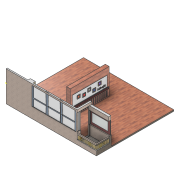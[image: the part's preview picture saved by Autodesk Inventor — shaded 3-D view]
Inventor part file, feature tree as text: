
AUTODESK INVENTOR PART (.ipt)
format: ipt  version: 2020.2 (Build 242310000, 310)  size: 1,721,344 bytes
history: native  units: mm
features: extrude x49, plane x45, sketch x36, other x4, loft x4, fillet x2, emboss x1
ambient origin geometry x8: Origin, YZ Plane, XZ Plane, XY Plane, X Axis, Y Axis, Z Axis, Center Point
bodies: Solid1 (feature_tree), Solid2 (feature_tree), Solid3 (feature_tree), Solid4 (feature_tree), Solid5 (feature_tree), Solid6 (feature_tree), Solid7 (feature_tree)
feature tree (141):
  extrude  "Extrusion1"  Depth=6000.0mm
  other  "Pod plane"
  other  "D. deo, terasa i prozori"
  plane  "Work Plane2"
  extrude  "Extrusion2"  TaperAngle=0.0deg  [1 undecoded]
  plane  "Work Plane3"
  sketch  "Sketch10"  dims[d22=100.0mm d23=100.0mm]
  extrude  "Extrusion3"  Depth=100.0mm
  extrude  "Extrusion4"  Depth=1000.0mm
  extrude  "Extrusion6"  Depth=1000.0mm
  extrude  "Extrusion7"  Depth=300.0mm
  extrude  "Extrusion8"  Depth=2000.0mm TaperAngle=0.0deg
  plane  "Work Plane4"
  plane  "Work Plane5"
  extrude  "Extrusion10"  Depth=150.0mm
  fillet  "Fillet1"  Radius=100.0mm
  plane  "Work Plane7"
  plane  "Work Plane8"
  extrude  "Extrusion11"  Depth=30.0mm
  plane  "Work Plane9"
  sketch  "Sketch15"  dims[d32=0.0mm d33=300.0mm]
  extrude  "Extrusion12"  Depth=10.0mm TaperAngle=0.0deg
  extrude  "Extrusion13"  Depth=50.0mm
  extrude  "Extrusion14"  Depth=50.0mm
  extrude  "Extrusion15"  Depth=25.0mm
  plane  "Work Plane10"
  plane  "Work Plane11"
  plane  "Work Plane12"
  sketch  "Sketch19"  dims[d93=40.0mm d94=30.0mm]
  extrude  "Extrusion18"  Depth=20.0mm TaperAngle=0.0deg
  extrude  "Extrusion19"  Depth=250.0mm TaperAngle=0.0deg
  plane  "Work Plane13"
  extrude  "Extrusion20"  TaperAngle=0.0deg  [1 undecoded]
  plane  "Work Plane14"
  extrude  "Extrusion21"  Depth=10.0mm
  plane  "Work Plane15"
  plane  "Work Plane16"
  extrude  "Extrusion22"  Depth=10.0mm
  plane  "Work Plane17"
  extrude  "Extrusion23"  Depth=200.0mm TaperAngle=0.0deg
  extrude  "Extrusion24"  TaperAngle=0.0deg  [1 undecoded]
  plane  "Work Plane18"
  plane  "Work Plane19"
  sketch  "Sketch28"  dims[d133=2.0mm d134=0.0mm d135=50.0mm]
  plane  "Work Plane20"
  extrude  "Extrusion25"  Depth=10.0mm
  extrude  "Extrusion26"  Depth=500.0mm TaperAngle=0.0deg
  plane  "Work Plane21"
  extrude  "Extrusion27"  Depth=250.0mm
  extrude  "Extrusion29"  Depth=250.0mm
  loft  "Loft1"
  loft  "Loft2"
  extrude  "Extrusion30"  Depth=5.0mm TaperAngle=0.0deg
  plane  "Work Plane22"
  plane  "Work Plane23"
  extrude  "Extrusion31"  TaperAngle=0.0deg  [1 undecoded]
  extrude  "Extrusion32"  Depth=20.0mm
  plane  "Work Plane24"
  loft  "Loft3"
  loft  "Loft4"
  extrude  "Extrusion33"  Depth=750.0mm TaperAngle=0.0deg
  extrude  "Extrusion34"  Depth=750.0mm
  plane  "Work Plane25"
  plane  "Work Plane26"
  plane  "Work Plane27"
  extrude  "Extrusion35"  Depth=30.0mm
  extrude  "Extrusion36"  Depth=15.0mm
  plane  "Work Plane28"
  extrude  "Extrusion37"  Depth=1000.0mm
  plane  "Work Plane29"
  extrude  "Extrusion38"  Depth=1550.0mm TaperAngle=0.0deg
  plane  "Work Plane30"
  extrude  "Extrusion39"  TaperAngle=0.0deg  [1 undecoded]
  plane  "Work Plane31"
  plane  "Work Plane32"
  plane  "Work Plane33"
  extrude  "Extrusion42"  Depth=42.5mm
  plane  "Work Plane34"
  sketch  "Sketch59"  dims[d182=250.0mm d187=250.0mm d188=250.0mm]
  plane  "Work Plane36"
  sketch  "Sketch60"  dims[d189=250.0mm d190=250.0mm d191=250.0mm d192=250.0mm]
  plane  "Work Plane37"
  extrude  "Extrusion43"  Depth=42.5mm
  extrude  "Extrusion44"  Depth=1500.0mm
  extrude  "Extrusion45"  Depth=132.5mm TaperAngle=0.0deg
  extrude  "Extrusion46"  TaperAngle=0.0deg  [1 undecoded]
  plane  "Work Plane38"
  extrude  "Extrusion47"  TaperAngle=0.0deg  [1 undecoded]
  plane  "Work Plane39"
  extrude  "Extrusion48"  Depth=20.0mm TaperAngle=0.0deg
  plane  "Work Plane40"
  extrude  "Extrusion49"  TaperAngle=0.0deg  [1 undecoded]
  plane  "Work Plane41"
  extrude  "Extrusion50"  Depth=600.0mm TaperAngle=0.0deg
  plane  "Work Plane42"
  extrude  "Extrusion51"  Depth=400.0mm
  plane  "Work Plane43"
  plane  "Work Plane47"
  extrude  "Extrusion55"  Depth=2250.0mm TaperAngle=0.0deg
  plane  "Work Plane48"
  extrude  "Extrusion56"  TaperAngle=0.0deg  [1 undecoded]
  plane  "Work Plane49"
  plane  "Work Plane50"
  extrude  "Extrusion57"  Depth=700.0mm
  plane  "Work Plane51"
  emboss  "Emboss1"
  sketch  "Sketch1"  dims[d0=7000.0mm d1=6000.0mm]
  sketch  "Sketch9"  dims[d2=100.0mm d3=0.0mm d7=0.0mm]
  sketch  "Sketch12"  dims[d24=1400.0mm d25=1000.0mm]
  sketch  "Sketch14"  dims[d26=1500.0mm d27=1000.0mm]
  sketch  "Sketch20"  dims[d129=150.0mm d131=10.0mm d132=0.0mm]
  sketch  "Sketch29"  dims[d136=50.0mm d137=50.0mm]
  sketch  "Sketch38"  dims[d138=25.0mm d141=25.0mm]
  sketch  "Sketch39"  dims[d142=250.0mm d143=0.0mm d144=20.0mm d145=0.0mm]
  sketch  "Sketch40"  dims[d146=30.0mm d147=250.0mm d148=0.0mm]
  sketch  "Sketch42"  dims[d149=0.0mm d162=0.0mm]
  sketch  "Sketch44"  dims[d163=10.0mm d164=10.0mm]
  other  "Edges2"
  other  "Edges1"
  sketch  "Sketch50"  dims[d165=120.0mm d166=10.0mm]
  sketch  "Sketch52"  dims[d167=10.0mm d168=200.0mm d169=0.0mm]
  sketch  "Sketch53"  dims[d170=20.0mm d172=0.0mm]
  sketch  "Sketch54"  dims[d173=0.0mm d174=10.0mm]
  sketch  "Sketch55"  dims[d177=10.0mm d178=500.0mm d179=0.0mm]
  sketch  "Sketch58"  dims[d180=0.0mm d181=250.0mm]
  sketch  "Sketch61"  dims[d193=250.0mm d194=250.0mm d195=15.0mm d196=0.0mm]
  sketch  "Sketch64"  dims[d197=5.0mm d198=0.0mm d199=5.0mm d200=0.0mm]
  sketch  "Sketch65"  dims[d201=15.0mm d202=0.0mm d203=0.0mm]
  sketch  "Sketch66"  dims[d204=30.0mm d205=25.0mm d206=25.0mm d207=50.0mm d208=50.0mm d209=50.0mm d210=150.0mm d211=30.0mm d212=40.0mm d213=100.0mm d214=150.0mm d216=0.0mm d217=20.0mm d218=0.0mm]
  sketch  "Sketch67"  dims[d219=10.0mm d220=10.0mm d221=10.0mm d222=120.0mm d223=10.0mm d225=0.0mm d226=200.0mm d227=20.0mm]
  sketch  "Sketch68"  dims[d228=0.0mm d229=150.0mm]
  sketch  "Sketch69"  dims[d230=100.0mm d231=200.0mm]
  sketch  "Sketch75"  dims[d232=750.0mm d233=0.0mm d234=750.0mm d235=0.0mm]
  sketch  "Sketch76"  dims[d236=0.0mm d237=750.0mm]
  sketch  "Sketch78"  dims[d238=75.0mm d239=30.0mm]
  sketch  "Sketch80"  dims[d240=30.0mm d241=15.0mm d242=1000.0mm d243=1550.0mm d244=0.0mm d245=0.0mm d247=42.5mm d248=42.5mm d249=1500.0mm d250=132.5mm d251=0.0mm d252=0.0mm d257=0.0mm d258=20.0mm d259=20.0mm d260=0.0mm d261=0.0mm d262=0.0mm d265=600.0mm d266=0.0mm d267=400.0mm d270=2250.0mm d271=0.0mm d272=0.0mm d278=700.0mm d280=100.0mm d281=100.0mm d282=1000.0mm d283=100.0mm d284=100.0mm d285=1000.0mm d286=1000.0mm d287=0.0mm d288=40.0mm d289=1400.0mm d290=0.0mm d291=20.0mm d292=20.0mm d293=1450.0mm d294=0.0mm d295=0.0mm d296=42.5mm d297=42.5mm d299=22.5mm d300=55.0mm d301=1500.0mm d302=0.0mm d305=1650.0mm d306=0.0mm d309=50.0mm d310=50.0mm d311=30.0mm d312=30.0mm d313=0.0mm d314=90.0deg d315=0.0mm d316=90.0deg d317=30.0mm d319=30.0mm d320=50.0mm d321=200.0mm d322=70.0mm d323=0.0mm d324=90.0deg d325=0.0mm d326=90.0deg d327=1500.0mm d328=0.0mm d329=0.0mm d330=0.0mm d331=150.0mm d332=10.0mm d333=0.0mm d334=150.0mm d335=10.0mm d336=0.0mm d337=950.0mm d338=0.0mm d339=90.0deg d340=0.0mm d341=90.0deg d342=0.0mm d343=90.0deg d344=0.0mm d345=90.0deg d346=30.0mm d347=30.0mm d348=0.0mm d349=0.0mm d350=70.0mm d351=70.0mm d352=250.0mm d353=0.0mm d354=250.0mm d362=750.0mm d374=0.0mm d375=95.0mm d376=120.0mm d377=3478.0mm d378=0.0mm d379=40.0mm d380=1500.0mm d381=0.0mm d382=0.0mm d383=843.0mm d384=0.0mm d385=0.0mm d386=50.0mm d387=0.0mm d388=60.0mm d389=0.0mm d390=1500.0mm d391=0.0mm d392=0.0mm d396=0.0mm d399=0.0mm d400=29.375mm d401=29.375mm d402=1500.0mm d403=40.0mm d404=0.0mm d405=0.0mm d407=75.0mm d425=20.0mm d427=0.0mm d428=75.0mm d429=100.0mm d430=0.0mm d431=75.0mm d432=100.0mm d433=1000.0mm d434=0.0mm d435=1500.0mm d436=0.0mm d437=20.0mm d438=20.0mm d439=20.0mm d440=20.0mm d441=20.0mm d442=20.0mm d443=20.0mm d444=20.0mm d445=20.0mm d446=20.0mm d448=20.0mm d461=350.0mm d462=0.0mm d463=60.0mm d464=60.0mm d465=1370.0mm d466=0.0mm d468=0.0mm d469=30.0mm d473=200.0mm d474=0.0mm d475=0.0mm d476=85.0mm d477=1518.0mm d478=60.0mm d479=0.0mm d480=0.0mm d481=0.0mm d482=300.0mm d483=0.0mm d484=0.0mm d485=95.0mm d486=1600.0mm d487=0.0mm d488=0.0mm d489=6.0mm d490=3250.0mm d491=0.0mm d492=0.0mm d506=0.0mm d507=100.0mm d508=120.0mm d509=3450.0mm d510=0.0mm d511=0.0mm d512=1.0mm d513=0.0mm d514=0.0mm d515=0.0mm d516=20.0mm d517=0.0mm d518=0.0mm d519=10.0mm d520=0.0mm d307=0.5mm d308=0.872665mm]
  sketch  "Sketch17"  dims[d37=0.0mm d41=150.0mm d91=100.0mm]
  fillet  "Fillet2"  Radius=100.0mm
  extrude  "Extrusion16"  Depth=100.0mm
  extrude  "Extrusion17"  Depth=1000.0mm
  sketch  "Sketch16"  dims[d34=3000.0mm d35=2000.0mm d36=0.0mm]
note: 9 required parameter values undecoded (feature->parameter linkage not recoverable at this tier; creation-order binding heuristic only, values carry confidence <= 0.55)
